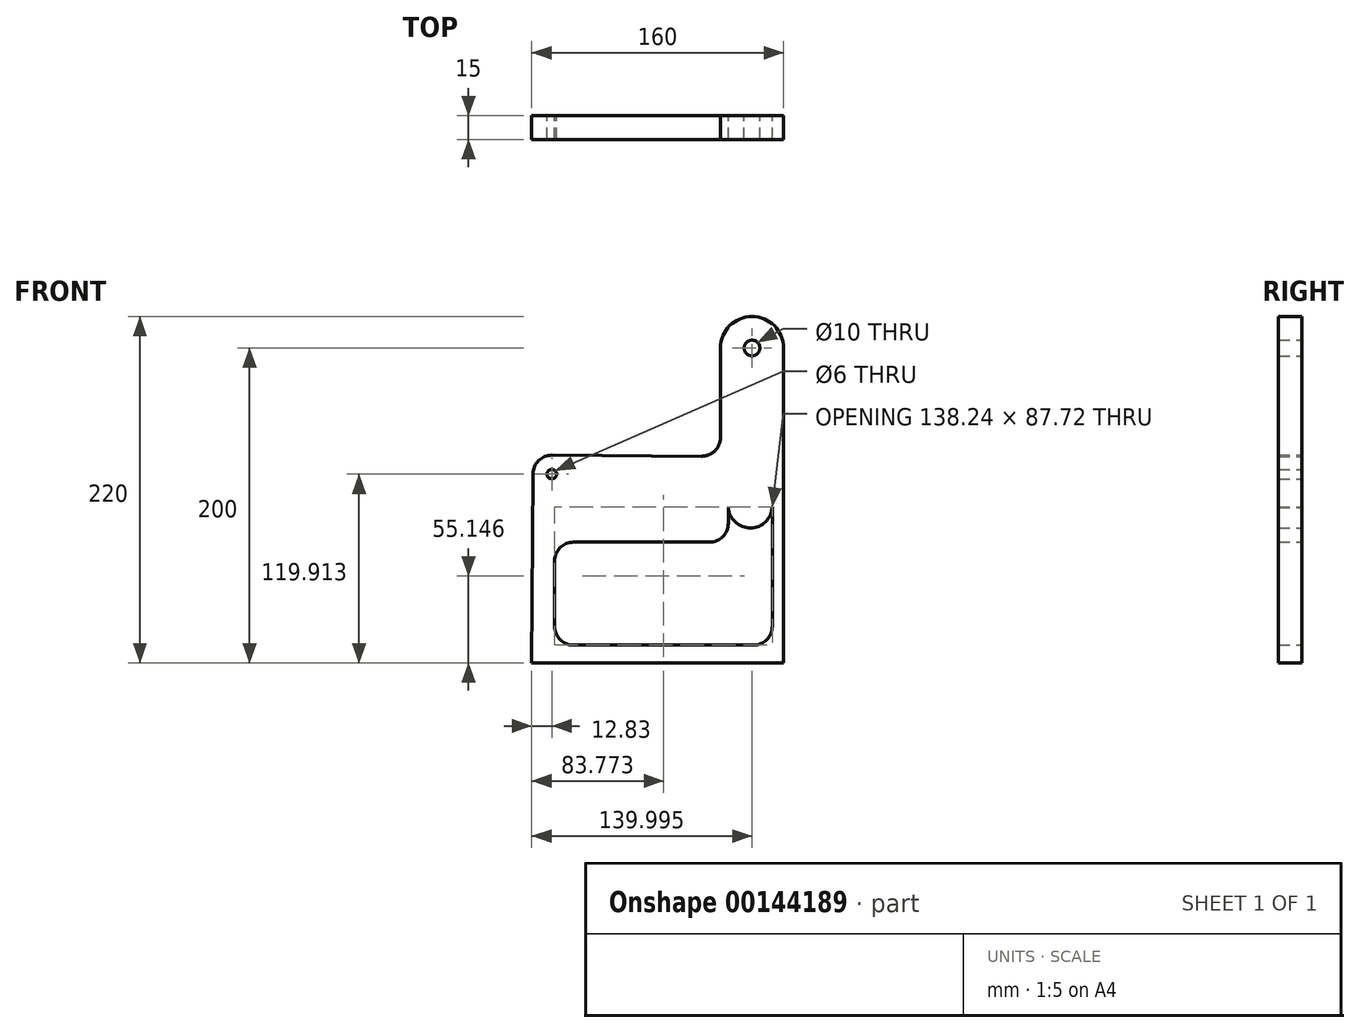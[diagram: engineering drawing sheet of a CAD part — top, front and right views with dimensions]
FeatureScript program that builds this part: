
annotation { "Feature Type Name" : "Feature", "Feature Type Description" : "" }
export const myFeature = defineFeature(function(context is Context, id is Id, definition is map)
    precondition{}
    {
        {
            var Q0;
            Q0=qCreatedBy(makeId("Front.planeOp"),FACE);
            var sketch = newSketch(context, id + "F0", { "sketchPlane" : qUnion([Q0])});
            skLineSegment(sketch, "E0", {"start": v(-26.45, 0) * mm, "end": v(-25.62, 120) * mm});
            skLineSegment(sketch, "E1", {"start": v(133.55, 0) * mm, "end": v(133.55, 200) * mm});
            skLineSegment(sketch, "E2", {"start": v(-26.45, 0) * mm, "end": v(133.55, 0) * mm});
            skCircle(sketch, "E3", {"center": v(113.55, 200) * mm, "radius": 5 * mm});
            skLineSegment(sketch, "E4", {"start": v(-13.54, 131.91) * mm, "end": v(81.46, 131.25) * mm});
            skLineSegment(sketch, "E5", {"start": v(93.55, 143.25) * mm, "end": v(93.55, 200) * mm});
            skArc(sketch, "E6", {"start": v(133.55, 200) * mm, "mid": v(113.55, 220) * mm, "end": v(93.55, 200) * mm});
            skPoint(sketch, "E7.visualSharp", {"position": v(-25.54, 132) * mm});
            skArc(sketch, "E7.filletArc", {"start": v(-13.54, 131.91) * mm, "mid": v(-22.05, 128.46) * mm, "end": v(-25.62, 120) * mm});
            skPoint(sketch, "E8.visualSharp", {"position": v(93.55, 131.17) * mm});
            skArc(sketch, "E8.filletArc", {"start": v(81.46, 131.25) * mm, "mid": v(90, 134.74) * mm, "end": v(93.55, 143.25) * mm});
            skCircle(sketch, "E9", {"center": v(-13.62, 119.91) * mm, "radius": 3 * mm});
            skArc(sketch, "E10", {"start": v(98.5, 98.68) * mm, "mid": v(112.62, 85.72) * mm, "end": v(126.44, 99) * mm});
            skLineSegment(sketch, "E11", {"start": v(126.44, 99) * mm, "end": v(126.44, 23.29) * mm});
            skLineSegment(sketch, "E12", {"start": v(114.44, 11.29) * mm, "end": v(0.2, 11.29) * mm});
            skLineSegment(sketch, "E13", {"start": v(-11.8, 23.29) * mm, "end": v(-11.8, 64.69) * mm});
            skLineSegment(sketch, "E14", {"start": v(0.2, 76.69) * mm, "end": v(86.5, 76.69) * mm});
            skLineSegment(sketch, "E15", {"start": v(98.5, 98.68) * mm, "end": v(98.5, 88.69) * mm});
            skPoint(sketch, "E16.visualSharp", {"position": v(-11.8, 76.69) * mm});
            skArc(sketch, "E16.filletArc", {"start": v(0.2, 76.69) * mm, "mid": v(-8.28, 73.17) * mm, "end": v(-11.8, 64.69) * mm});
            skPoint(sketch, "E17.visualSharp", {"position": v(98.5, 76.69) * mm});
            skArc(sketch, "E17.filletArc", {"start": v(86.5, 76.69) * mm, "mid": v(94.98, 80.2) * mm, "end": v(98.5, 88.69) * mm});
            skPoint(sketch, "E18.visualSharp", {"position": v(-11.8, 11.29) * mm});
            skArc(sketch, "E18.filletArc", {"start": v(-11.8, 23.29) * mm, "mid": v(-8.28, 14.8) * mm, "end": v(0.2, 11.29) * mm});
            skPoint(sketch, "E19.visualSharp", {"position": v(126.44, 11.29) * mm});
            skArc(sketch, "E19.filletArc", {"start": v(114.44, 11.29) * mm, "mid": v(122.93, 14.8) * mm, "end": v(126.44, 23.29) * mm});
            skSolve(sketch);
        }
        {
            var Q0;
            Q0 = qSketchRegion(id + "F0", true);
            extrude(context, id + "F1", {"entities" : qUnion([Q0]), "depth" : 15 * mm});
        }
    });
